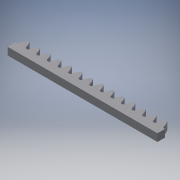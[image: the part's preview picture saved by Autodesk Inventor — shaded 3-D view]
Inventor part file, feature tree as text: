
AUTODESK INVENTOR PART (.ipt)
format: ipt  version: 2017 (Build 210142000, 142)  size: 179,712 bytes
history: native  units: mm
features: sketch x2, extrude x2, pattern_linear x1
ambient origin geometry x8: Origin, YZ Plane, XZ Plane, XY Plane, X Axis, Y Axis, Z Axis, Center Point
bodies: Body1 (feature_tree)
feature tree (5):
  sketch  "Sketch1"  dims[d2=100.0mm d3=10.0mm]
  extrude  "Extrusion2"  Depth=10.0mm
  extrude  "Extrusion3"  Depth=5.0mm
  pattern_linear  "Rectangular Pattern1"  Spacing1=0.0mm  [1 undecoded]
  sketch  "Sketch2"  dims[d4=5.0mm d5=0.0mm d6=5.0mm d7=0.0mm d8=0.0mm d9=150.0mm d11=7.065mm]
note: 1 required parameter value undecoded (feature->parameter linkage not recoverable at this tier; creation-order binding heuristic only, values carry confidence <= 0.55)
